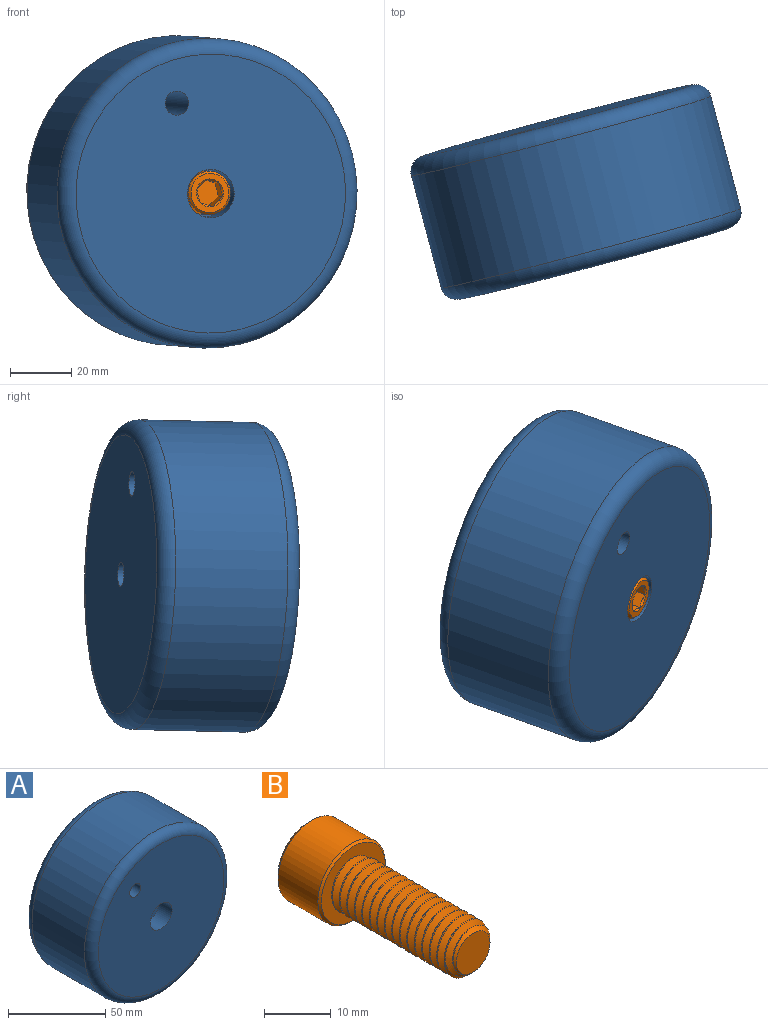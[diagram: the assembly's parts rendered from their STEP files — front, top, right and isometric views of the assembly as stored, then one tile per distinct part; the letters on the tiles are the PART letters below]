
ASSEMBLY  parts=2 mates=1
PART A: 9 faces, bbox 110x48.3x110 mm
  f0: cylinder r=50.8mm len=101.6mm, axis (0,1,0), area 12161mm2, adj f3,f4
  f1: plane 91.44x91.44mm, normal (0,-1,0), area 6319.5mm2, adj f4,f7,f8
  f2: plane 91.44x91.44mm, normal (0,1,0), area 6468mm2, adj f3,f5,f8
  f3: torus R=45.72mm, axis (0,-1,0), area 2454.4mm2, adj f0,f2
  f4: torus R=45.72mm, axis (0,-1,0), area 2454.4mm2, adj f0,f1
  f5: cylinder r=3.97mm len=38.74mm, axis (0,-1,0), area 965.9mm2, adj f2,f6
  f6: plane 15.88x15.88mm, normal (0,-1,0), area 148.4mm2, adj f5,f7
  f7: cylinder r=7.94mm len=15.88mm, axis (0,-1,0), area 475mm2, adj f1,f6
  f8: cylinder r=3.97mm len=48.26mm, axis (0,-1,0), area 1203.4mm2, adj f1,f2
PART B: 24 faces, bbox 16x37.3x16 mm
  f0: cylinder r=4.76mm len=24.21mm, axis (0,-1,0), area 148.6mm2, adj f2,f4,f5,f6
  f1: plane 7.14x7.14mm, normal (0,-1,0), area 40.1mm2, adj f2
  f2: cone r=3.57mm half-angle=45deg, axis (0,1,0), area 24.1mm2, adj f0,f1,f3,f4,f5
  f3: cylinder r=3.73mm len=25.24mm, axis (0,1,0), area 72mm2, adj f2,f4,f5,f6
  f4: bspline ~26.26x11mm, area 494.7mm2, adj f0,f2,f3,f6
  f5: bspline ~26.79x11mm, area 493.3mm2, adj f0,f2,f3,f6
  f6: plane 14.2x14.2mm, normal (0,-1,0), area 87.6mm2, adj f0,f3,f4,f5,f23
  f7: cylinder r=7.14mm len=14.29mm, axis (0,-1,0), area 379.4mm2, adj f22,f23
  f8: plane 12.86x12.86mm, normal (0,1,0), area 63.9mm2, adj f9,f10,f11,f12,f13,f14,f22
  f9: cone r=4.58mm half-angle=45deg, axis (0,1,0), area 0mm2, adj f8,f16
  f10: cone r=4.58mm half-angle=45deg, axis (0,1,0), area 0mm2, adj f8,f17
  f11: cone r=4.58mm half-angle=45deg, axis (0,1,0), area 0mm2, adj f8,f18
  f12: cone r=4.58mm half-angle=45deg, axis (0,1,0), area 0mm2, adj f8,f19
  f13: cone r=4.58mm half-angle=45deg, axis (0,1,0), area 0mm2, adj f8,f20
  f14: cone r=4.58mm half-angle=45deg, axis (0,1,0), area 0mm2, adj f8,f21
  f15: plane 9.17x7.94mm, normal (0,1,0), area 54.6mm2, adj f16,f17,f18,f19,f20,f21
  f16: plane 7.69x5.71mm, normal (-0.5,0,-0.87), area 25.4mm2, adj f9,f15,f17,f21
  f17: plane 7.69x6.33mm, normal (-1,0,0), area 25.4mm2, adj f10,f15,f16,f18
  f18: plane 7.69x5.71mm, normal (-0.5,0,0.87), area 25.4mm2, adj f11,f15,f17,f19
  f19: plane 7.69x5.71mm, normal (0.5,0,0.87), area 25.4mm2, adj f12,f15,f18,f20
  f20: plane 7.69x6.33mm, normal (1,0,0), area 25.4mm2, adj f13,f15,f19,f21
  f21: plane 7.69x5.71mm, normal (0.5,0,-0.87), area 25.4mm2, adj f14,f15,f16,f20
  f22: cone r=6.43mm half-angle=45deg, axis (0,-1,0), area 43.1mm2, adj f7,f8
  f23: cone r=7.14mm half-angle=45deg, axis (0,1,0), area 22.1mm2, adj f6,f7
PLACE A rot(axis=(-0.03,0.71,0.7),21.2deg) t=(-59.58,-148.41,9.39)mm
PLACE B rot(axis=(0.61,0.09,-0.79),169deg) t=(-56.43,-161.37,9.29)mm
MATE planar A.f5 <-> B.f6  axis (0.26,-0.97,-0.02) through (-49.67,-185.84,8.52)mm
